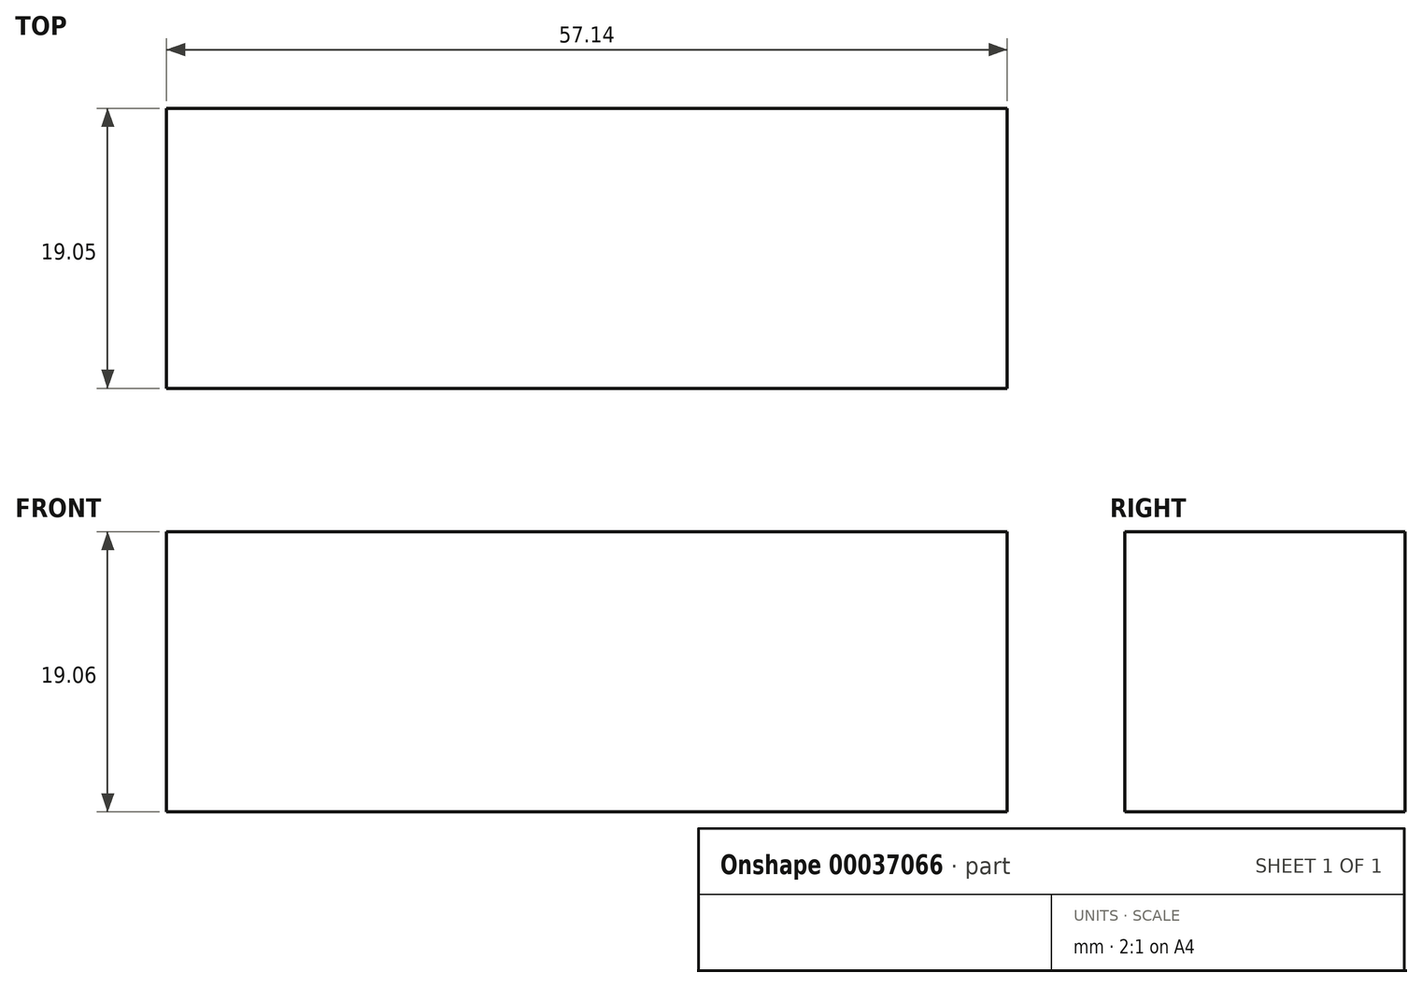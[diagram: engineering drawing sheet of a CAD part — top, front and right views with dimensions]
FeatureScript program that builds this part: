
annotation { "Feature Type Name" : "Feature", "Feature Type Description" : "" }
export const myFeature = defineFeature(function(context is Context, id is Id, definition is map)
    precondition{}
    {
        {
            var Q0;
            Q0=qCreatedBy(makeId("Front.planeOp"),FACE);
            var sketch = newSketch(context, id + "F0", { "sketchPlane" : qUnion([Q0])});
            skLineSegment(sketch, "E0.rect.bottom", {"start": v(28.58, 9.53) * mm, "end": v(-28.58, 9.53) * mm});
            skLineSegment(sketch, "E0.rect.top", {"start": v(28.57, -9.53) * mm, "end": v(-28.57, -9.53) * mm});
            skLineSegment(sketch, "E0.rect.left", {"start": v(28.58, 9.53) * mm, "end": v(28.58, -9.52) * mm});
            skLineSegment(sketch, "E0.rect.right", {"start": v(-28.58, 9.53) * mm, "end": v(-28.58, -9.52) * mm});
            skPoint(sketch, "E0.rect.middle", {"position": v(0, 0) * mm});
            skSolve(sketch);
        }
        {
            var Q0;
            Q0 = qSketchRegion(id + "F0", true);
            extrude(context, id + "F1", {"entities" : qUnion([Q0]), "depth" : 19.05 * mm});
        }
    });
